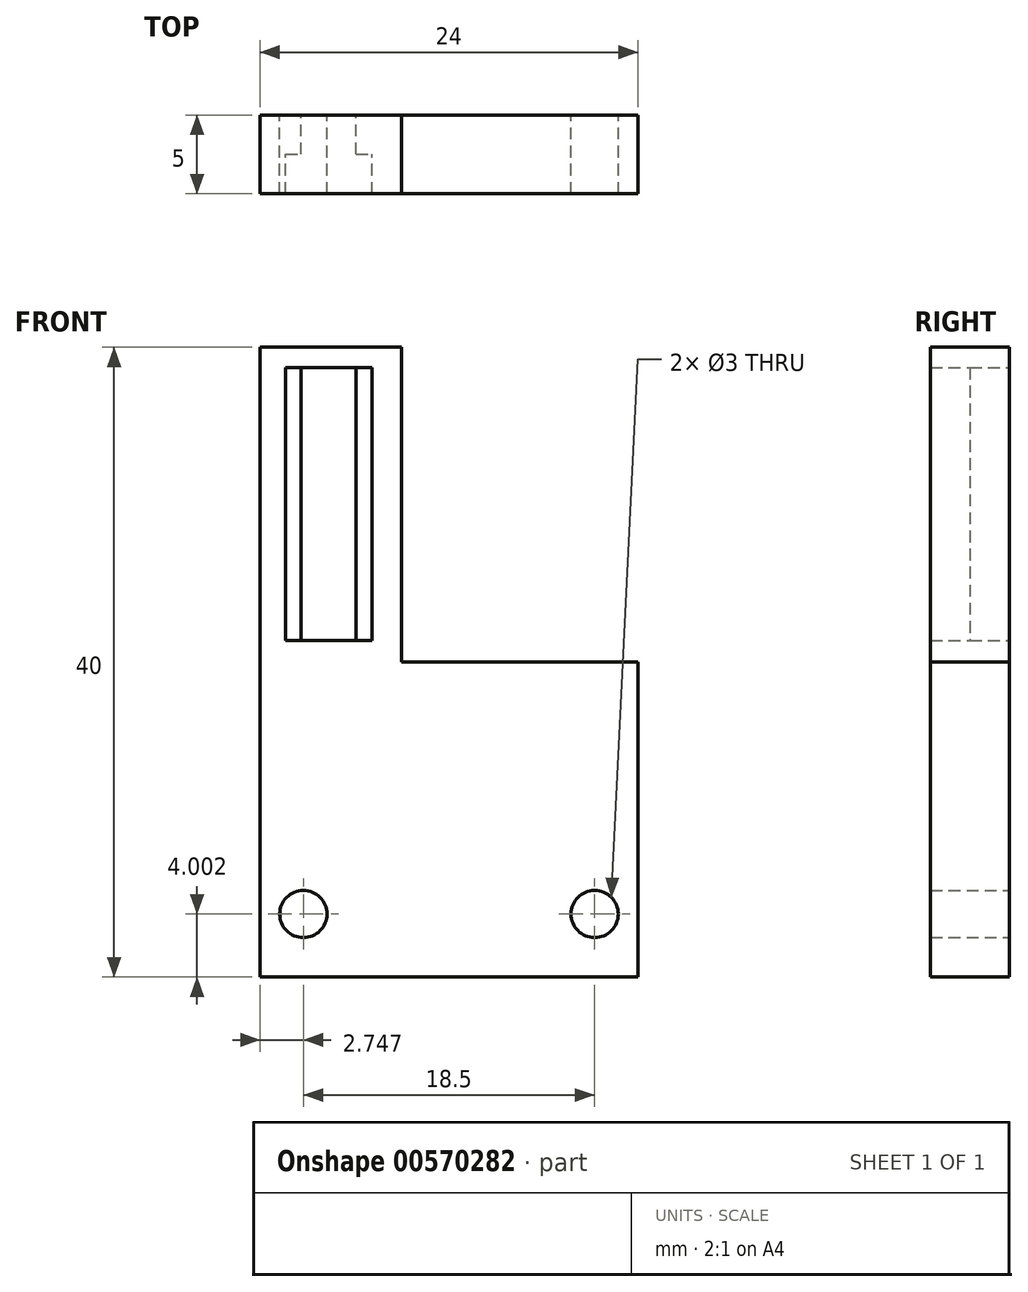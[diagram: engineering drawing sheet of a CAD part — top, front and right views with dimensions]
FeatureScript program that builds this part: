
annotation { "Feature Type Name" : "Feature", "Feature Type Description" : "" }
export const myFeature = defineFeature(function(context is Context, id is Id, definition is map)
    precondition{}
    {
        {
            var Q0;
            Q0=qCreatedBy(makeId("Front.planeOp"),FACE);
            var sketch = newSketch(context, id + "F0", { "sketchPlane" : qUnion([Q0])});
            skLineSegment(sketch, "E0.bottom", {"start": v(-11.28, 13.42) * mm, "end": v(12.72, 13.42) * mm});
            skLineSegment(sketch, "E0.top", {"start": v(-11.28, -6.58) * mm, "end": v(12.72, -6.58) * mm});
            skLineSegment(sketch, "E0.left", {"start": v(-11.28, 13.42) * mm, "end": v(-11.28, -6.58) * mm});
            skLineSegment(sketch, "E0.right", {"start": v(12.72, 13.42) * mm, "end": v(12.72, -6.58) * mm});
            skLineSegment(sketch, "E1", {"start": v(-11.28, -6.58) * mm, "end": v(-8.53, -6.58) * mm});
            skLineSegment(sketch, "E2", {"start": v(-8.53, -6.58) * mm, "end": v(-8.53, -2.58) * mm});
            skCircle(sketch, "E3", {"center": v(-8.53, -2.58) * mm, "radius": 1.5 * mm});
            skLineSegment(sketch, "E4.bottom", {"start": v(-11.28, 13.42) * mm, "end": v(-2.28, 13.42) * mm});
            skLineSegment(sketch, "E4.top", {"start": v(-11.28, 33.42) * mm, "end": v(-2.28, 33.42) * mm});
            skLineSegment(sketch, "E4.left", {"start": v(-11.28, 13.42) * mm, "end": v(-11.28, 33.42) * mm});
            skLineSegment(sketch, "E4.right", {"start": v(-2.28, 13.42) * mm, "end": v(-2.28, 33.42) * mm});
            skLineSegment(sketch, "E5.bottom", {"start": v(-9.66, 32.13) * mm, "end": v(-4.16, 32.13) * mm});
            skLineSegment(sketch, "E5.top", {"start": v(-9.66, 14.78) * mm, "end": v(-4.16, 14.78) * mm});
            skLineSegment(sketch, "E5.left", {"start": v(-9.66, 32.13) * mm, "end": v(-9.66, 14.78) * mm});
            skLineSegment(sketch, "E5.right", {"start": v(-4.16, 32.13) * mm, "end": v(-4.16, 14.78) * mm});
            skLineSegment(sketch, "E6.bottom", {"start": v(-8.69, 32.13) * mm, "end": v(-5.19, 32.13) * mm});
            skLineSegment(sketch, "E6.top", {"start": v(-8.69, 14.78) * mm, "end": v(-5.19, 14.78) * mm});
            skLineSegment(sketch, "E6.left", {"start": v(-8.69, 32.13) * mm, "end": v(-8.69, 14.78) * mm});
            skLineSegment(sketch, "E6.right", {"start": v(-5.19, 32.13) * mm, "end": v(-5.19, 14.78) * mm});
            skLineSegment(sketch, "E7", {"start": v(12.72, -6.58) * mm, "end": v(9.97, -6.58) * mm});
            skLineSegment(sketch, "E8", {"start": v(9.97, -6.58) * mm, "end": v(9.97, 3.32) * mm});
            skLineSegment(sketch, "E9", {"start": v(9.97, -6.58) * mm, "end": v(-8.53, -6.58) * mm});
            skLineSegment(sketch, "E10", {"start": v(0.72, -6.58) * mm, "end": v(0.72, -0.78) * mm});
            skCircle(sketch, "E11.MirrorC", {"center": v(9.97, -2.58) * mm, "radius": 1.5 * mm});
            skSolve(sketch);
        }
        {
            var Q0;
            Q0 = qSketchRegion(id + "F0", true);
            extrude(context, id + "F1", {"entities" : qUnion([Q0]), "depth" : 5 * mm, "offsetDistance" : 25.4 * mm});
        }
        {
            var Q0;
            {var subQ0=sQuery(id+"F0.wireOp",EDGE,"E5.left");Q0=makeQuery(id+"F0.imprint","IMPRINT",FACE,{"disambiguationData":[TD([[makeQuery(id+"F0.imprint","IMPRINT",EDGE,{"derivedFrom":subQ0}),1.0]])]});}
            var Q1;
            {var subQ0=sQuery(id+"F0.wireOp",EDGE,"E5.right");Q1=makeQuery(id+"F0.imprint","IMPRINT",FACE,{"disambiguationData":[TD([[makeQuery(id+"F0.imprint","IMPRINT",EDGE,{"derivedFrom":subQ0}),-1.0]])]});}
            extrude(context, id + "F2", {"entities" : qUnion([Q0, Q1]), "operationType" : NewBodyOperationType.ADD, "depth" : 2.5 * mm, "offsetDistance" : 25.4 * mm});
        }
    });
